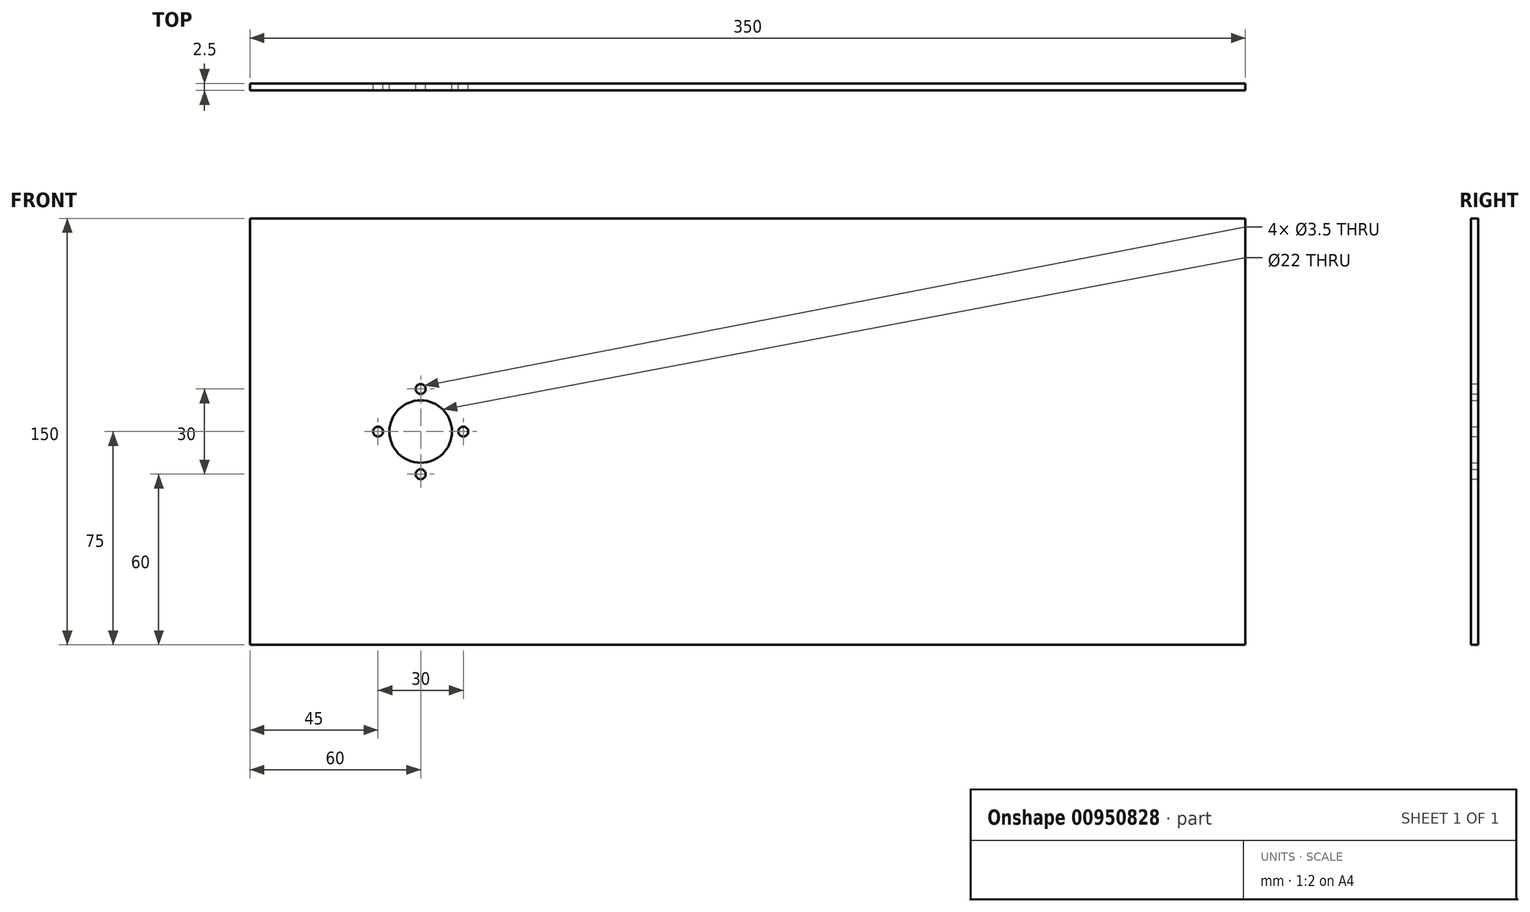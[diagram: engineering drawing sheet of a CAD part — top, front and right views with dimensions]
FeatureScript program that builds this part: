
annotation { "Feature Type Name" : "Feature", "Feature Type Description" : "" }
export const myFeature = defineFeature(function(context is Context, id is Id, definition is map)
    precondition{}
    {
        {
            var Q0;
            Q0=qCreatedBy(makeId("Front.planeOp"),FACE);
            var sketch = newSketch(context, id + "F0", { "sketchPlane" : qUnion([Q0])});
            skLineSegment(sketch, "E0.bottom", {"start": v(175, 75) * mm, "end": v(-175, 75) * mm});
            skLineSegment(sketch, "E0.top", {"start": v(175, -75) * mm, "end": v(-175, -75) * mm});
            skLineSegment(sketch, "E0.left", {"start": v(175, 75) * mm, "end": v(175, -75) * mm});
            skLineSegment(sketch, "E0.right", {"start": v(-175, 75) * mm, "end": v(-175, -75) * mm});
            skPoint(sketch, "E0.middle", {"position": v(0, 0) * mm});
            skCircle(sketch, "E1", {"center": v(-115, 0) * mm, "radius": 11 * mm});
            skCircle(sketch, "E2", {"center": v(-130, 0) * mm, "radius": 1.75 * mm});
            skCircle(sketch, "E3.1.0", {"center": v(-115, -15) * mm, "radius": 1.75 * mm});
            skCircle(sketch, "E3.2.0", {"center": v(-100, 0) * mm, "radius": 1.75 * mm});
            skCircle(sketch, "E3.3.0", {"center": v(-115, 15) * mm, "radius": 1.75 * mm});
            skSolve(sketch);
        }
        {
            var Q0;
            Q0=qSketchRegion(id+"F0",true);
            extrude(context, id + "F1", {"entities" : qUnion([Q0]), "depth" : 2.5 * mm, "offsetDistance" : 25 * mm});
        }
    });
